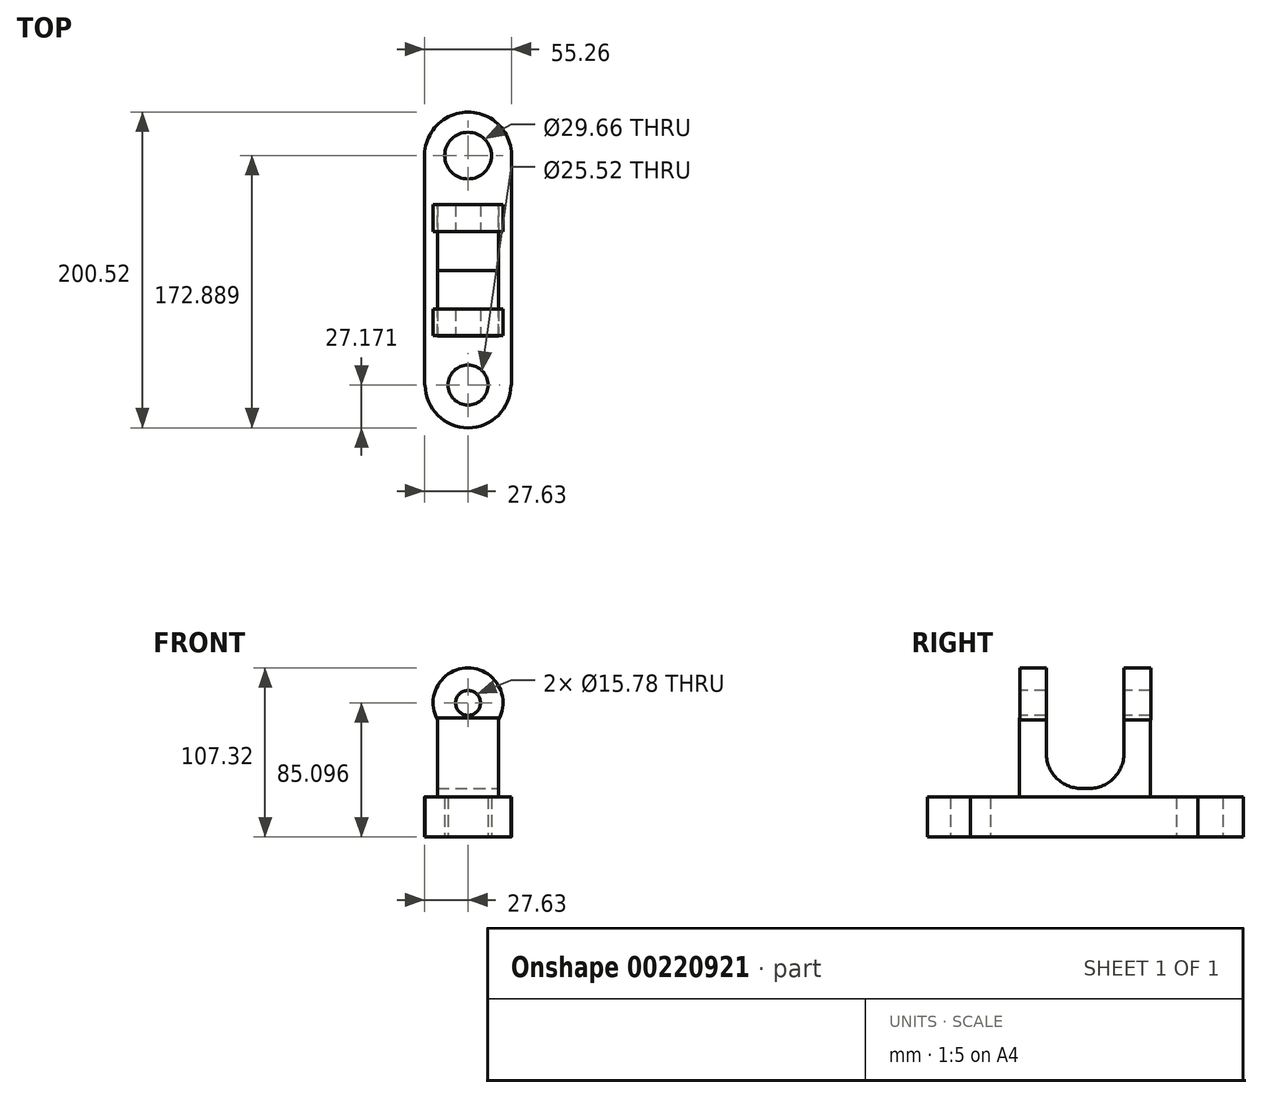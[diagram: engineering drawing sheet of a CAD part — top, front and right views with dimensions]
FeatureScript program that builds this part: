
annotation { "Feature Type Name" : "Feature", "Feature Type Description" : "" }
export const myFeature = defineFeature(function(context is Context, id is Id, definition is map)
    precondition{}
    {
        {
            var Q0;
            Q0=qCreatedBy(makeId("Top.planeOp"),FACE);
            var sketch = newSketch(context, id + "F0", { "sketchPlane" : qUnion([Q0])});
            skLineSegment(sketch, "E0.bottom", {"start": v(-14.83, 72.86) * mm, "end": v(14.83, 72.86) * mm});
            skLineSegment(sketch, "E0.top", {"start": v(-27.6, -72.86) * mm, "end": v(-27.17, -72.86) * mm});
            skLineSegment(sketch, "E0.left", {"start": v(-27.6, 72.86) * mm, "end": v(-27.6, -72.86) * mm});
            skLineSegment(sketch, "E0.right", {"start": v(27.6, 72.86) * mm, "end": v(27.6, -72.86) * mm});
            skPoint(sketch, "E0.middle", {"position": v(0, 0) * mm});
            skArc(sketch, "E1", {"start": v(27.6, 71.75) * mm, "mid": v(0, 100.5) * mm, "end": v(-27.6, 71.75) * mm});
            skArc(sketch, "E2", {"start": v(-27.17, -72.86) * mm, "mid": v(0, -100.03) * mm, "end": v(27.17, -72.86) * mm});
            skCircle(sketch, "E3", {"center": v(0, -72.86) * mm, "radius": 12.76 * mm});
            skCircle(sketch, "E4", {"center": v(0, 72.86) * mm, "radius": 14.83 * mm});
            skLineSegment(sketch, "E5.trimOffspring", {"start": v(27.17, -72.86) * mm, "end": v(27.6, -72.86) * mm});
            skLineSegment(sketch, "E6.trimOffspring", {"start": v(-12.76, -72.86) * mm, "end": v(12.76, -72.86) * mm});
            skSolve(sketch);
        }
        {
            var Q0;
            Q0 = qSketchRegion(id + "F0", true);
            extrude(context, id + "F1", {"entities" : qUnion([Q0]), "depth" : 25.4 * mm});
        }
        {
            var Q0;
            Q0=makeQuery(id+"F1.opExtrude","CAP_FACE",FACE,{"disambiguationData":[OSD([sQuery(id+"F0.wireOp",EDGE,"E0.top"),sQuery(id+"F0.wireOp",EDGE,"E0.left"),sQuery(id+"F0.wireOp",EDGE,"E0.right"),sQuery(id+"F0.wireOp",EDGE,"E1"),sQuery(id+"F0.wireOp",EDGE,"E2"),sQuery(id+"F0.wireOp",EDGE,"E3"),sQuery(id+"F0.wireOp",EDGE,"E4"),sQuery(id+"F0.wireOp",EDGE,"E5.trimOffspring")])],"isStart":false});
            var sketch = newSketch(context, id + "F2", { "sketchPlane" : qUnion([Q0])});
            skLineSegment(sketch, "E7.bottom", {"start": v(19.48, -41.62) * mm, "end": v(-19.48, -41.62) * mm});
            skLineSegment(sketch, "E7.top", {"start": v(19.48, 41.62) * mm, "end": v(-19.48, 41.62) * mm});
            skLineSegment(sketch, "E7.left", {"start": v(19.48, -41.62) * mm, "end": v(19.48, 41.62) * mm});
            skLineSegment(sketch, "E7.right", {"start": v(-19.48, -41.62) * mm, "end": v(-19.48, 41.62) * mm});
            skPoint(sketch, "E7.middle", {"position": v(0, 0) * mm});
            skSolve(sketch);
        }
        {
            var Q0;
            Q0=makeQuery(id+"F2.imprint","IMPRINT",FACE,{"disambiguationData":[TD([[makeQuery(id+"F2.imprint","IMPRINT",EDGE,{"derivedFrom":sQuery(id+"F2.wireOp",EDGE,"E7.bottom")}),-1.0]])]});
            extrude(context, id + "F3", {"entities" : qUnion([Q0]), "operationType" : NewBodyOperationType.ADD, "depth" : 50.04 * mm});
        }
        {
            var Q0;
            Q0=makeQuery(id+"F3.opExtrude","SWEPT_FACE",FACE,{"disambiguationData":[OSD([sQuery(id+"F2.wireOp",EDGE,"E7.bottom")])]});
            var sketch = newSketch(context, id + "F4", { "sketchPlane" : qUnion([Q0])});
            skSolve(sketch);
        }
        {
            var Q0;
            {var subQ0=sQuery(id+"F2.wireOp",EDGE,"E7.bottom");Q0=makeQuery(id+"F4.imprint","IMPRINT",FACE,{"disambiguationData":[TD([[makeQuery(id+"F4.imprint","IMPRINT",EDGE,{"derivedFrom":makeQuery(id+"F3.opExtrude","CAP_EDGE",EDGE,{"disambiguationData":[OSD([subQ0])],"isStart":false})}),1.0]])]});}
            var sketch = newSketch(context, id + "F5", { "sketchPlane" : qUnion([Q0])});
            skCircle(sketch, "E8", {"center": v(0, 85.1) * mm, "radius": 22.22 * mm});
            skCircle(sketch, "E9", {"center": v(0, 85.1) * mm, "radius": 7.9 * mm});
            skSolve(sketch);
        }
        {
            var Q0;
            Q0=makeQuery(id+"F5.imprint","IMPRINT",FACE,{"disambiguationData":[TD([[makeQuery(id+"F5.imprint","IMPRINT",EDGE,{"derivedFrom":sQuery(id+"F5.wireOp",EDGE,"E9")}),-1.0]])]});
            extrude(context, id + "F6", {"entities" : qUnion([Q0]), "operationType" : NewBodyOperationType.ADD, "oppositeDirection" : true, "depth" : 83.31 * mm, "hasSecondDirection" : true, "secondDirectionOppositeDirection" : true, "secondDirectionDepth" : 0.25 * mm});
        }
        {
            var Q0;
            Q0=makeQuery(id+"F3.opExtrude","SWEPT_FACE",FACE,{"disambiguationData":[OSD([sQuery(id+"F2.wireOp",EDGE,"E7.left")])]});
            var sketch = newSketch(context, id + "F7", { "sketchPlane" : qUnion([Q0])});
            skLineSegment(sketch, "E10", {"start": v(24.72, 108.5) * mm, "end": v(24.72, 53) * mm});
            skLineSegment(sketch, "E11", {"start": v(-24.63, 108.17) * mm, "end": v(-24.63, 53) * mm});
            skLineSegment(sketch, "E12", {"start": v(-24.63, 108.17) * mm, "end": v(24.72, 108.5) * mm});
            skArc(sketch, "E13", {"start": v(-24.63, 53) * mm, "mid": v(-17.25, 36.46) * mm, "end": v(0, 30.89) * mm});
            skArc(sketch, "E14", {"start": v(0, 30.89) * mm, "mid": v(17.3, 36.42) * mm, "end": v(24.72, 53) * mm});
            skSolve(sketch);
        }
        {
            var Q0;
            {var subQ0=sQuery(id+"F7.wireOp",EDGE,"E13");Q0=makeQuery(id+"F7.imprint","IMPRINT",FACE,{"disambiguationData":[TD([[makeQuery(id+"F7.imprint","IMPRINT",EDGE,{"derivedFrom":subQ0}),1.0]])]});}
            var Q1;
            {var subQ0=sQuery(id+"F7.wireOp",EDGE,"E12");Q1=makeQuery(id+"F7.imprint","IMPRINT",FACE,{"disambiguationData":[TD([[makeQuery(id+"F7.imprint","IMPRINT",EDGE,{"derivedFrom":subQ0}),-1.0]])]});}
            extrude(context, id + "F8", {"entities" : qUnion([Q0, Q1]), "operationType" : NewBodyOperationType.REMOVE, "endBound" : BoundingType.THROUGH_ALL, "oppositeDirection" : true, "depth" : 25.4 * mm, "hasSecondDirection" : true, "secondDirectionBound" : SecondDirectionBoundingType.THROUGH_ALL, "secondDirectionOppositeDirection" : false, "secondDirectionDepth" : 25.4 * mm});
        }
    });
